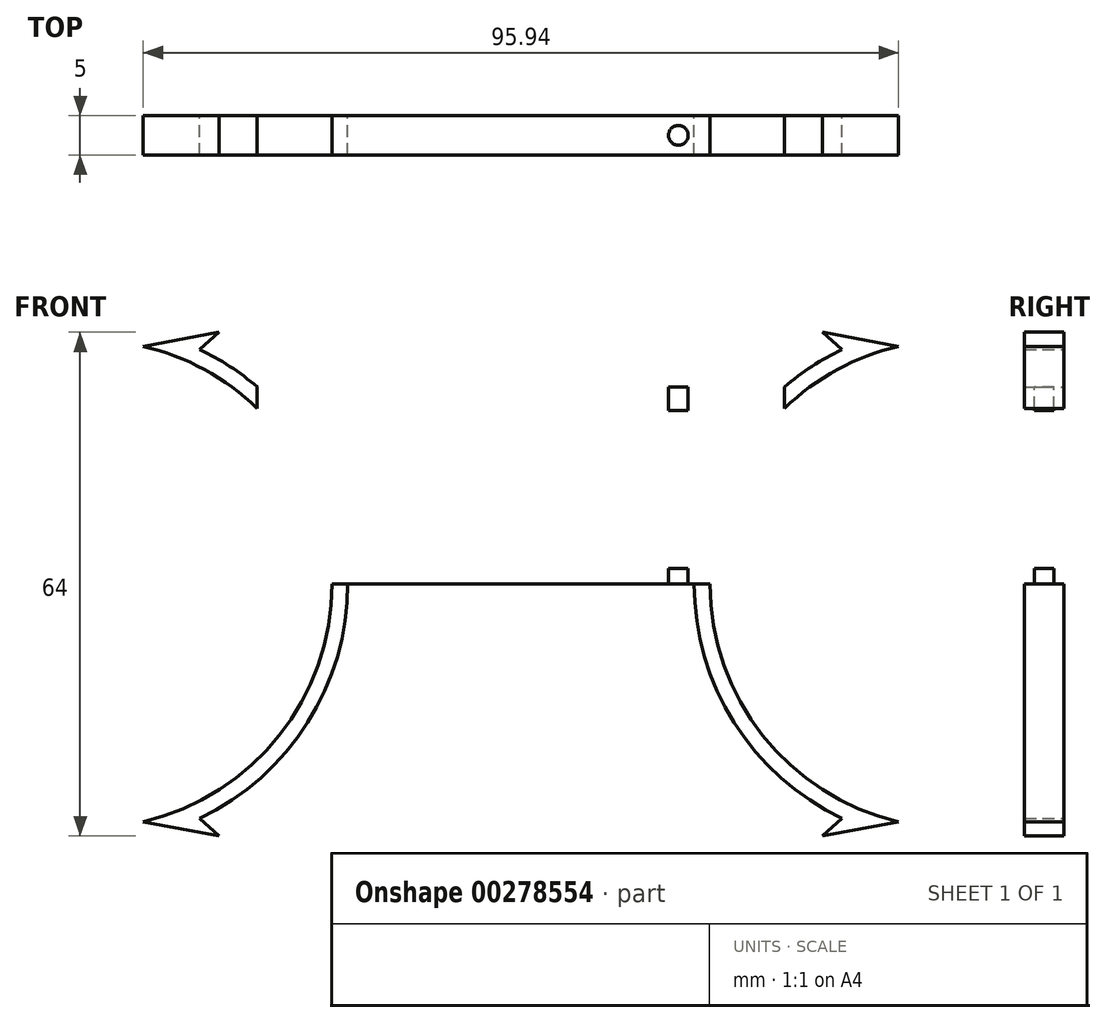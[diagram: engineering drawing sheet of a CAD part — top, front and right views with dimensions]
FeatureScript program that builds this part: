
annotation { "Feature Type Name" : "Feature", "Feature Type Description" : "" }
export const myFeature = defineFeature(function(context is Context, id is Id, definition is map)
    precondition{}
    {
        {
            var Q0;
            Q0=qCreatedBy(makeId("Front.planeOp"),FACE);
            var sketch = newSketch(context, id + "F0", { "sketchPlane" : qUnion([Q0])});
            skLineSegment(sketch, "E0", {"start": v(-55, 31) * mm, "end": v(-55, -31) * mm, "construction": true});
            skLineSegment(sketch, "E1", {"start": v(0, 0) * mm, "end": v(-55, 0) * mm, "construction": true});
            skPoint(sketch, "E1.endSnap0", {"position": v(-55, 0) * mm});
            skArc(sketch, "E2", {"start": v(-47.97, -30.2) * mm, "mid": v(-24, 0) * mm, "end": v(-47.97, 30.2) * mm});
            skArc(sketch, "E3", {"start": v(-40.8, -29.79) * mm, "mid": v(-27.1, -17.61) * mm, "end": v(-22, 0) * mm});
            skLineSegment(sketch, "E4", {"start": v(-55, -31) * mm, "end": v(-55, -33) * mm});
            skLineSegment(sketch, "E5", {"start": v(-55, 31) * mm, "end": v(-55, 33) * mm});
            skLineSegment(sketch, "E6", {"start": v(0, 0) * mm, "end": v(0, 25.02) * mm, "construction": true});
            skLineSegment(sketch, "E7", {"start": v(0, 25.02) * mm, "end": v(-33.49, 25.02) * mm});
            skLineSegment(sketch, "E8", {"start": v(0, 22.02) * mm, "end": v(-30.42, 22.02) * mm});
            skArc(sketch, "E9.trimOffspring", {"start": v(-33.49, 25.02) * mm, "mid": v(-36.98, 27.65) * mm, "end": v(-40.8, 29.79) * mm});
            skLineSegment(sketch, "E10", {"start": v(0, 2) * mm, "end": v(-22.06, 2) * mm});
            skLineSegment(sketch, "E11", {"start": v(0, 0) * mm, "end": v(-22, 0) * mm});
            skArc(sketch, "E12.trimOffspring", {"start": v(-22.06, 2) * mm, "mid": v(-24.55, 12.72) * mm, "end": v(-30.42, 22.02) * mm});
            skLineSegment(sketch, "E13", {"start": v(-47.97, 30.2) * mm, "end": v(-38.31, 32) * mm});
            skPoint(sketch, "E13.endSnap0", {"position": v(-55, 32) * mm});
            skLineSegment(sketch, "E14", {"start": v(-38.31, 32) * mm, "end": v(-40.8, 29.79) * mm});
            skLineSegment(sketch, "E15.MirrorCS", {"start": v(-38.31, -32) * mm, "end": v(-40.8, -29.79) * mm});
            skLineSegment(sketch, "E16.MirrorCS", {"start": v(-47.97, -30.2) * mm, "end": v(-38.31, -32) * mm});
            skLineSegment(sketch, "E17", {"start": v(-22, 0) * mm, "end": v(0, 0) * mm});
            skLineSegment(sketch, "E18.MirrorCS", {"start": v(0, 0) * mm, "end": v(55, 0) * mm, "construction": true});
            skLineSegment(sketch, "E19.MirrorCS", {"start": v(0, 2) * mm, "end": v(22.06, 2) * mm});
            skLineSegment(sketch, "E20.MirrorCS", {"start": v(0, 22.02) * mm, "end": v(30.42, 22.02) * mm});
            skLineSegment(sketch, "E21.MirrorCS", {"start": v(0, 25.02) * mm, "end": v(33.49, 25.02) * mm});
            skArc(sketch, "E22.MirrorCS", {"start": v(33.49, 25.02) * mm, "mid": v(36.98, 27.65) * mm, "end": v(40.8, 29.79) * mm});
            skLineSegment(sketch, "E23.MirrorCS", {"start": v(38.31, 32) * mm, "end": v(40.8, 29.79) * mm});
            skLineSegment(sketch, "E24.MirrorCS", {"start": v(47.97, 30.2) * mm, "end": v(38.31, 32) * mm});
            skArc(sketch, "E25.MirrorCS", {"start": v(47.97, -30.2) * mm, "mid": v(24, 0) * mm, "end": v(47.97, 30.2) * mm});
            skArc(sketch, "E26.MirrorCS", {"start": v(22.06, 2) * mm, "mid": v(24.55, 12.72) * mm, "end": v(30.42, 22.02) * mm});
            skArc(sketch, "E27.MirrorCS", {"start": v(40.8, -29.79) * mm, "mid": v(27.1, -17.61) * mm, "end": v(22, 0) * mm});
            skLineSegment(sketch, "E28.MirrorCS", {"start": v(47.97, -30.2) * mm, "end": v(38.31, -32) * mm});
            skLineSegment(sketch, "E29.MirrorCS", {"start": v(38.31, -32) * mm, "end": v(40.8, -29.79) * mm});
            skLineSegment(sketch, "E30.MirrorCS", {"start": v(55, 31) * mm, "end": v(55, 33) * mm});
            skLineSegment(sketch, "E31.MirrorCS", {"start": v(55, -31) * mm, "end": v(55, -33) * mm});
            skPoint(sketch, "E32.orphan", {"position": v(55, 33) * mm});
            skPoint(sketch, "E33.orphan", {"position": v(55, 31) * mm});
            skPoint(sketch, "E34.orphan", {"position": v(55, -31) * mm});
            skPoint(sketch, "E35.orphan", {"position": v(55, -33) * mm});
            skLineSegment(sketch, "E36", {"start": v(0, 0) * mm, "end": v(22, 0) * mm});
            skSolve(sketch);
        }
        {
            var Q0;
            Q0=makeQuery(id+"F0.imprint","IMPRINT",FACE,{"disambiguationData":[TD([[makeQuery(id+"F0.imprint","IMPRINT",EDGE,{"derivedFrom":sQuery(id+"F0.wireOp",EDGE,"E2")}),-1.0]])]});
            extrude(context, id + "F1", {"entities" : qUnion([Q0]), "depth" : 5 * mm});
        }
        {
            var Q0;
            Q0=makeQuery(id+"F1.opExtrude","SWEPT_FACE",FACE,{"disambiguationData":[OSD([sQuery(id+"F0.wireOp",EDGE,"E7"),sQuery(id+"F0.wireOp",EDGE,"E21.MirrorCS")])]});
            var sketch = newSketch(context, id + "F2", { "sketchPlane" : qUnion([Q0])});
            skCircle(sketch, "E37", {"center": v(0, -2.5) * mm, "radius": 1.25 * mm});
            skPoint(sketch, "E37.centerSnap0", {"position": v(0, -5) * mm});
            skLineSegment(sketch, "E38", {"start": v(-33.49, -2.5) * mm, "end": v(33.49, -2.5) * mm, "construction": true});
            skCircle(sketch, "E39", {"center": v(-20, -2.5) * mm, "radius": 1.25 * mm});
            skCircle(sketch, "E40.MirrorC", {"center": v(20, -2.5) * mm, "radius": 1.25 * mm});
            skSolve(sketch);
        }
        {
            var Q0;
            Q0=makeQuery(id+"F2.imprint","IMPRINT",FACE,{"disambiguationData":[TD([[makeQuery(id+"F2.imprint","IMPRINT",EDGE,{"derivedFrom":sQuery(id+"F2.wireOp",EDGE,"E39")}),1.0]])]});
            var Q1;
            Q1=makeQuery(id+"F2.imprint","IMPRINT",FACE,{"disambiguationData":[TD([[makeQuery(id+"F2.imprint","IMPRINT",EDGE,{"derivedFrom":sQuery(id+"F2.wireOp",EDGE,"E37")}),1.0]])]});
            var Q2;
            Q2=makeQuery(id+"F2.imprint","IMPRINT",FACE,{"disambiguationData":[TD([[makeQuery(id+"F2.imprint","IMPRINT",EDGE,{"derivedFrom":sQuery(id+"F2.wireOp",EDGE,"E40.MirrorC")}),-1.0]])]});
            extrude(context, id + "F3", {"entities" : qUnion([Q0, Q1, Q2]), "operationType" : NewBodyOperationType.REMOVE, "oppositeDirection" : true, "depth" : 25 * mm});
        }
    });
